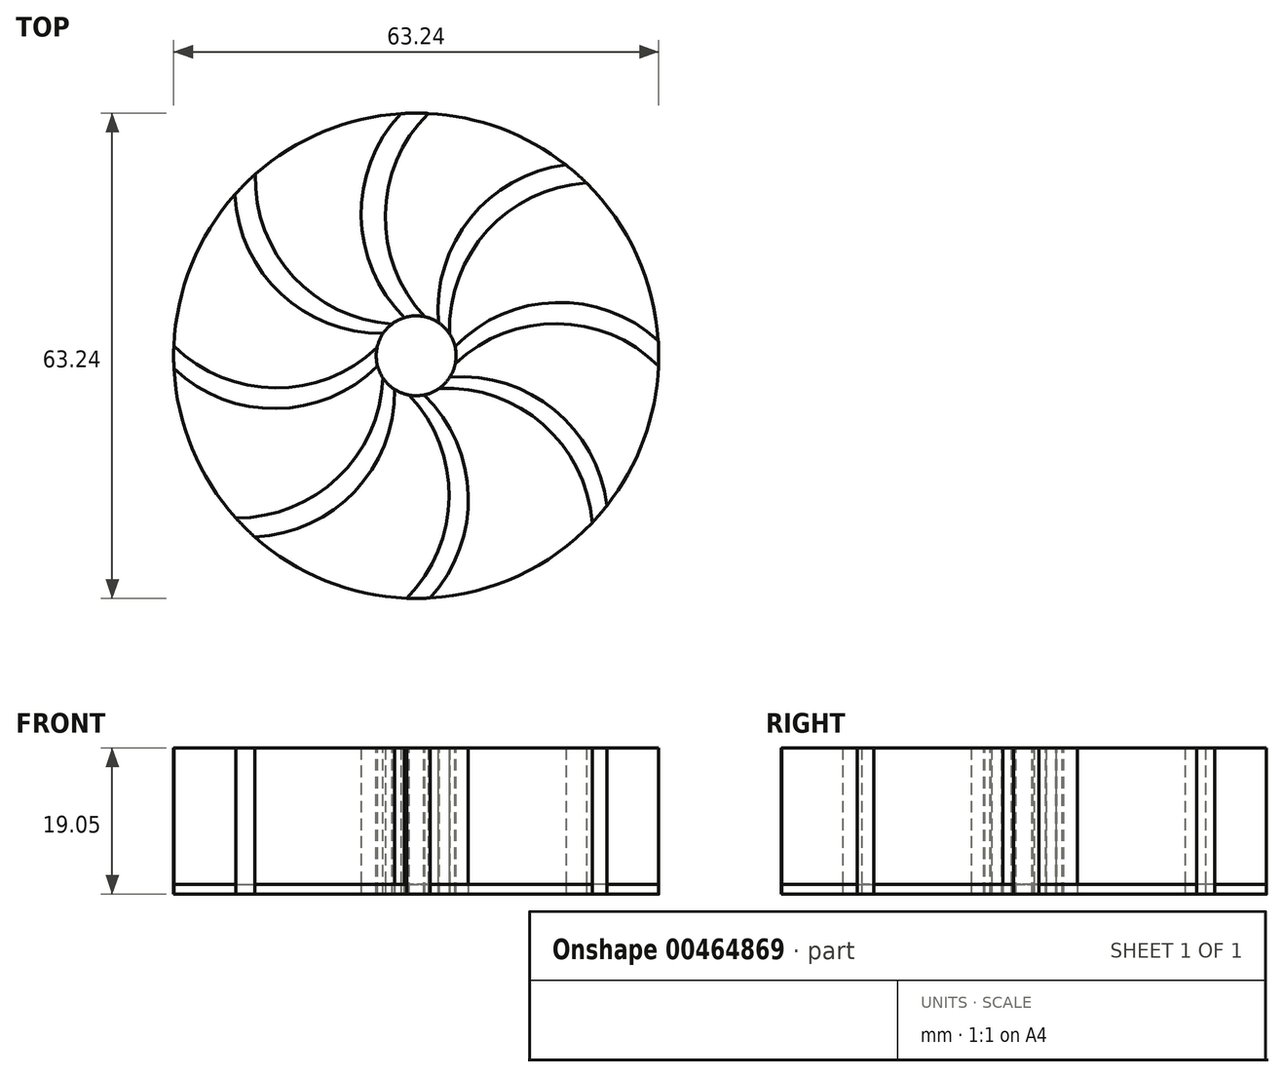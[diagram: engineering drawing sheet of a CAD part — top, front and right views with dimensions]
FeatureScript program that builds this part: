
annotation { "Feature Type Name" : "Feature", "Feature Type Description" : "" }
export const myFeature = defineFeature(function(context is Context, id is Id, definition is map)
    precondition{}
    {
        {
            var Q0;
            Q0=qCreatedBy(makeId("Top.planeOp"),FACE);
            var sketch = newSketch(context, id + "F0", { "sketchPlane" : qUnion([Q0])});
            skCircle(sketch, "E0", {"center": v(0, 0) * mm, "radius": 5.08 * mm});
            skPoint(sketch, "E1", {"position": v(-3.6, 3.6) * mm});
            skPoint(sketch, "E2", {"position": v(3.6, 3.6) * mm});
            skPoint(sketch, "E3", {"position": v(3.6, -3.6) * mm});
            skPoint(sketch, "E4", {"position": v(-3.6, -3.6) * mm});
            skArc(sketch, "E5", {"start": v(-31.6, 1.3) * mm, "mid": v(-18.28, -4.18) * mm, "end": v(-4.93, 1.22) * mm});
            skArc(sketch, "E6", {"start": v(-31.58, -1.67) * mm, "mid": v(-18.16, -6.88) * mm, "end": v(-4.93, -1.22) * mm});
            skArc(sketch, "E7", {"start": v(-31.58, -1.67) * mm, "mid": v(-29.22, -12.1) * mm, "end": v(-23.52, -21.13) * mm});
            skArc(sketch, "E8", {"start": v(-31.6, 1.3) * mm, "mid": v(-31.62, -0.19) * mm, "end": v(-31.58, -1.67) * mm});
            skArc(sketch, "E9", {"start": v(-23.52, -21.13) * mm, "mid": v(-22.31, -22.4) * mm, "end": v(-21.03, -23.61) * mm});
            skArc(sketch, "E10", {"start": v(-23.52, -21.13) * mm, "mid": v(-10.16, -15.82) * mm, "end": v(-4.32, -2.67) * mm});
            skArc(sketch, "E11", {"start": v(-21.03, -23.61) * mm, "mid": v(-11.82, -29.33) * mm, "end": v(-1.23, -31.6) * mm});
            skArc(sketch, "E12", {"start": v(-21.03, -23.61) * mm, "mid": v(-7.97, -17.64) * mm, "end": v(-2.8, -4.24) * mm});
            skLineSegment(sketch, "E13", {"start": v(-1.23, -31.6) * mm, "end": v(-1.23, -31.6) * mm});
            skArc(sketch, "E14", {"start": v(-1.23, -31.6) * mm, "mid": v(0.3, -31.62) * mm, "end": v(1.84, -31.57) * mm});
            skArc(sketch, "E15", {"start": v(-1.23, -31.6) * mm, "mid": v(4.3, -18.32) * mm, "end": v(-1.04, -4.97) * mm});
            skArc(sketch, "E16", {"start": v(1.84, -31.57) * mm, "mid": v(6.78, -18.1) * mm, "end": v(0.92, -5) * mm});
            skLineSegment(sketch, "E17", {"start": v(1.84, -31.57) * mm, "end": v(1.84, -31.57) * mm});
            skArc(sketch, "E18", {"start": v(1.84, -31.57) * mm, "mid": v(13.33, -28.67) * mm, "end": v(22.96, -21.75) * mm});
            skArc(sketch, "E19", {"start": v(22.96, -21.75) * mm, "mid": v(23.93, -20.68) * mm, "end": v(24.85, -19.56) * mm});
            skArc(sketch, "E20", {"start": v(22.96, -21.75) * mm, "mid": v(16.45, -8.87) * mm, "end": v(2.79, -4.25) * mm});
            skArc(sketch, "E21", {"start": v(24.85, -19.56) * mm, "mid": v(17.94, -7) * mm, "end": v(4.23, -2.82) * mm});
            skArc(sketch, "E22", {"start": v(24.85, -19.56) * mm, "mid": v(29.66, -10.97) * mm, "end": v(31.6, -1.32) * mm});
            skArc(sketch, "E23", {"start": v(31.56, 1.96) * mm, "mid": v(28.78, 13.11) * mm, "end": v(22.2, 22.53) * mm});
            skLineSegment(sketch, "E24", {"start": v(31.56, 1.96) * mm, "end": v(31.56, 1.96) * mm});
            skArc(sketch, "E25", {"start": v(31.56, 1.96) * mm, "mid": v(18.09, 6.95) * mm, "end": v(4.96, 1.1) * mm});
            skArc(sketch, "E26", {"start": v(22.2, 22.53) * mm, "mid": v(9.2, 16.2) * mm, "end": v(4.37, 2.58) * mm});
            skArc(sketch, "E27", {"start": v(22.2, 22.53) * mm, "mid": v(20.89, 23.74) * mm, "end": v(19.52, 24.88) * mm});
            skArc(sketch, "E28", {"start": v(19.52, 24.88) * mm, "mid": v(11.07, 29.62) * mm, "end": v(1.58, 31.58) * mm});
            skArc(sketch, "E29", {"start": v(19.52, 24.88) * mm, "mid": v(7.02, 17.88) * mm, "end": v(2.94, 4.14) * mm});
            skArc(sketch, "E30", {"start": v(-2.02, 31.56) * mm, "mid": v(-12.16, 29.2) * mm, "end": v(-20.98, 23.66) * mm});
            skArc(sketch, "E31", {"start": v(1.58, 31.58) * mm, "mid": v(-0.22, 31.62) * mm, "end": v(-2.02, 31.56) * mm});
            skArc(sketch, "E32", {"start": v(1.58, 31.58) * mm, "mid": v(-4.02, 18.32) * mm, "end": v(1.26, 4.92) * mm});
            skArc(sketch, "E33", {"start": v(-2.02, 31.56) * mm, "mid": v(-7.17, 18.1) * mm, "end": v(-1.41, 4.88) * mm});
            skLineSegment(sketch, "E34", {"start": v(-20.98, 23.66) * mm, "end": v(-20.98, 23.66) * mm});
            skArc(sketch, "E35", {"start": v(-20.98, 23.66) * mm, "mid": v(-15.93, 10.23) * mm, "end": v(-2.94, 4.14) * mm});
            skArc(sketch, "E36", {"start": v(-20.98, 23.66) * mm, "mid": v(-22.35, 22.37) * mm, "end": v(-23.64, 21) * mm});
            skArc(sketch, "E37", {"start": v(-23.64, 21) * mm, "mid": v(-17.57, 8) * mm, "end": v(-4.15, 2.93) * mm});
            skArc(sketch, "E38", {"start": v(-23.64, 21) * mm, "mid": v(-29.32, 11.84) * mm, "end": v(-31.6, 1.3) * mm});
            skArc(sketch, "E39", {"start": v(31.6, -1.32) * mm, "mid": v(31.62, 0.32) * mm, "end": v(31.56, 1.96) * mm});
            skArc(sketch, "E40", {"start": v(31.6, -1.32) * mm, "mid": v(18.3, 4.2) * mm, "end": v(4.94, -1.17) * mm});
            skSolve(sketch);
        }
        {
            var Q0;
            {var subQ0=sQuery(id+"F0.wireOp",EDGE,"E35");Q0=makeQuery(id+"F0.imprint","IMPRINT",FACE,{"disambiguationData":[TD([[makeQuery(id+"F0.imprint","IMPRINT",EDGE,{"derivedFrom":subQ0}),-1.0]])]});}
            var Q1;
            Q1=makeQuery(id+"F0.imprint","IMPRINT",FACE,{"disambiguationData":[TD([[makeQuery(id+"F0.imprint","IMPRINT",EDGE,{"derivedFrom":sQuery(id+"F0.wireOp",EDGE,"E31")}),1.0]])]});
            var Q2;
            {var subQ0=sQuery(id+"F0.wireOp",EDGE,"E26");Q2=makeQuery(id+"F0.imprint","IMPRINT",FACE,{"disambiguationData":[TD([[makeQuery(id+"F0.imprint","IMPRINT",EDGE,{"derivedFrom":subQ0}),-1.0]])]});}
            var Q3;
            {var subQ0=sQuery(id+"F0.wireOp",EDGE,"E25");Q3=makeQuery(id+"F0.imprint","IMPRINT",FACE,{"disambiguationData":[TD([[makeQuery(id+"F0.imprint","IMPRINT",EDGE,{"derivedFrom":subQ0}),1.0]])]});}
            var Q4;
            Q4=makeQuery(id+"F0.imprint","IMPRINT",FACE,{"disambiguationData":[TD([[makeQuery(id+"F0.imprint","IMPRINT",EDGE,{"derivedFrom":sQuery(id+"F0.wireOp",EDGE,"E19")}),1.0]])]});
            var Q5;
            Q5=makeQuery(id+"F0.imprint","IMPRINT",FACE,{"disambiguationData":[TD([[makeQuery(id+"F0.imprint","IMPRINT",EDGE,{"derivedFrom":sQuery(id+"F0.wireOp",EDGE,"E14")}),1.0]])]});
            var Q6;
            Q6=makeQuery(id+"F0.imprint","IMPRINT",FACE,{"disambiguationData":[TD([[makeQuery(id+"F0.imprint","IMPRINT",EDGE,{"derivedFrom":sQuery(id+"F0.wireOp",EDGE,"E9")}),1.0]])]});
            var Q7;
            {var subQ0=sQuery(id+"F0.wireOp",EDGE,"E5");Q7=makeQuery(id+"F0.imprint","IMPRINT",FACE,{"disambiguationData":[TD([[makeQuery(id+"F0.imprint","IMPRINT",EDGE,{"derivedFrom":subQ0}),-1.0]])]});}
            extrude(context, id + "F1", {"entities" : qUnion([Q0, Q1, Q2, Q3, Q4, Q5, Q6, Q7]), "depth" : 19.05 * mm});
        }
        {
            var Q0;
            {var subQ0=sQuery(id+"F0.wireOp",EDGE,"E5");Q0=makeQuery(id+"F0.imprint","IMPRINT",FACE,{"disambiguationData":[TD([[makeQuery(id+"F0.imprint","IMPRINT",EDGE,{"derivedFrom":subQ0}),1.0]])]});}
            var Q1;
            Q1=makeQuery(id+"F0.imprint","IMPRINT",FACE,{"disambiguationData":[TD([[makeQuery(id+"F0.imprint","IMPRINT",EDGE,{"derivedFrom":sQuery(id+"F0.wireOp",EDGE,"E30")}),1.0]])]});
            var Q2;
            Q2=makeQuery(id+"F0.imprint","IMPRINT",FACE,{"disambiguationData":[TD([[makeQuery(id+"F0.imprint","IMPRINT",EDGE,{"derivedFrom":sQuery(id+"F0.wireOp",EDGE,"E28")}),1.0]])]});
            var Q3;
            Q3=makeQuery(id+"F0.imprint","IMPRINT",FACE,{"disambiguationData":[TD([[makeQuery(id+"F0.imprint","IMPRINT",EDGE,{"derivedFrom":sQuery(id+"F0.wireOp",EDGE,"E23")}),1.0]])]});
            var Q4;
            {var subQ0=sQuery(id+"F0.wireOp",EDGE,"E21");Q4=makeQuery(id+"F0.imprint","IMPRINT",FACE,{"disambiguationData":[TD([[makeQuery(id+"F0.imprint","IMPRINT",EDGE,{"derivedFrom":subQ0}),-1.0]])]});}
            var Q5;
            {var subQ0=sQuery(id+"F0.wireOp",EDGE,"E16");Q5=makeQuery(id+"F0.imprint","IMPRINT",FACE,{"disambiguationData":[TD([[makeQuery(id+"F0.imprint","IMPRINT",EDGE,{"derivedFrom":subQ0}),-1.0]])]});}
            var Q6;
            Q6=makeQuery(id+"F0.imprint","IMPRINT",FACE,{"disambiguationData":[TD([[makeQuery(id+"F0.imprint","IMPRINT",EDGE,{"derivedFrom":sQuery(id+"F0.wireOp",EDGE,"E11")}),1.0]])]});
            var Q7;
            {var subQ0=sQuery(id+"F0.wireOp",EDGE,"E6");Q7=makeQuery(id+"F0.imprint","IMPRINT",FACE,{"disambiguationData":[TD([[makeQuery(id+"F0.imprint","IMPRINT",EDGE,{"derivedFrom":subQ0}),-1.0]])]});}
            extrude(context, id + "F2", {"entities" : qUnion([Q0, Q1, Q2, Q3, Q4, Q5, Q6, Q7]), "depth" : 1.27 * mm});
        }
        {
            var Q0;
            Q0=makeQuery(id+"F1.opExtrude","CAP_FACE",FACE,{"disambiguationData":[OSD([sQuery(id+"F0.wireOp",EDGE,"E0"),sQuery(id+"F0.wireOp",EDGE,"E5"),sQuery(id+"F0.wireOp",EDGE,"E6"),sQuery(id+"F0.wireOp",EDGE,"E8")])],"isStart":false});
            var sketch = newSketch(context, id + "F3", { "sketchPlane" : qUnion([Q0])});
            skCircle(sketch, "E41", {"center": v(0, 0) * mm, "radius": 5.2 * mm});
            skSolve(sketch);
        }
        {
            var Q0;
            Q0=sQuery(id+"F3.wireOp",VERTEX,"E41.center");
            var Q1;
            Q1=makeQuery(id+"F1.opExtrude","SWEPT_BODY",BODY,{"disambiguationData":[OSD([sQuery(id+"F0.wireOp",EDGE,"E0"),sQuery(id+"F0.wireOp",EDGE,"E26"),sQuery(id+"F0.wireOp",EDGE,"E27"),sQuery(id+"F0.wireOp",EDGE,"E29")])]});
            var Q2;
            Q2=makeQuery(id+"F1.opExtrude","SWEPT_BODY",BODY,{"disambiguationData":[OSD([sQuery(id+"F0.wireOp",EDGE,"E0"),sQuery(id+"F0.wireOp",EDGE,"E31"),sQuery(id+"F0.wireOp",EDGE,"E32"),sQuery(id+"F0.wireOp",EDGE,"E33")])]});
            var Q3;
            Q3=makeQuery(id+"F1.opExtrude","SWEPT_BODY",BODY,{"disambiguationData":[OSD([sQuery(id+"F0.wireOp",EDGE,"E0"),sQuery(id+"F0.wireOp",EDGE,"E35"),sQuery(id+"F0.wireOp",EDGE,"E36"),sQuery(id+"F0.wireOp",EDGE,"E37")])]});
            var Q4;
            Q4=makeQuery(id+"F1.opExtrude","SWEPT_BODY",BODY,{"disambiguationData":[OSD([sQuery(id+"F0.wireOp",EDGE,"E0"),sQuery(id+"F0.wireOp",EDGE,"E5"),sQuery(id+"F0.wireOp",EDGE,"E6"),sQuery(id+"F0.wireOp",EDGE,"E8")])]});
            var Q5;
            Q5=makeQuery(id+"F1.opExtrude","SWEPT_BODY",BODY,{"disambiguationData":[OSD([sQuery(id+"F0.wireOp",EDGE,"E0"),sQuery(id+"F0.wireOp",EDGE,"E9"),sQuery(id+"F0.wireOp",EDGE,"E10"),sQuery(id+"F0.wireOp",EDGE,"E12")])]});
            var Q6;
            Q6=makeQuery(id+"F1.opExtrude","SWEPT_BODY",BODY,{"disambiguationData":[OSD([sQuery(id+"F0.wireOp",EDGE,"E0"),sQuery(id+"F0.wireOp",EDGE,"E14"),sQuery(id+"F0.wireOp",EDGE,"E15"),sQuery(id+"F0.wireOp",EDGE,"E16")])]});
            var Q7;
            Q7=makeQuery(id+"F1.opExtrude","SWEPT_BODY",BODY,{"disambiguationData":[OSD([sQuery(id+"F0.wireOp",EDGE,"E0"),sQuery(id+"F0.wireOp",EDGE,"E19"),sQuery(id+"F0.wireOp",EDGE,"E20"),sQuery(id+"F0.wireOp",EDGE,"E21")])]});
            var Q8;
            Q8=makeQuery(id+"F1.opExtrude","SWEPT_BODY",BODY,{"disambiguationData":[OSD([sQuery(id+"F0.wireOp",EDGE,"E0"),sQuery(id+"F0.wireOp",EDGE,"E25"),sQuery(id+"F0.wireOp",EDGE,"E39"),sQuery(id+"F0.wireOp",EDGE,"E40")])]});
            var Q9;
            Q9=makeQuery(id+"F2.opExtrude","SWEPT_BODY",BODY,{"disambiguationData":[OSD([sQuery(id+"F0.wireOp",EDGE,"E0"),sQuery(id+"F0.wireOp",EDGE,"E23"),sQuery(id+"F0.wireOp",EDGE,"E25"),sQuery(id+"F0.wireOp",EDGE,"E26")])]});
            var Q10;
            Q10=makeQuery(id+"F2.opExtrude","SWEPT_BODY",BODY,{"disambiguationData":[OSD([sQuery(id+"F0.wireOp",EDGE,"E0"),sQuery(id+"F0.wireOp",EDGE,"E28"),sQuery(id+"F0.wireOp",EDGE,"E29"),sQuery(id+"F0.wireOp",EDGE,"E32")])]});
            var Q11;
            Q11=makeQuery(id+"F2.opExtrude","SWEPT_BODY",BODY,{"disambiguationData":[OSD([sQuery(id+"F0.wireOp",EDGE,"E0"),sQuery(id+"F0.wireOp",EDGE,"E30"),sQuery(id+"F0.wireOp",EDGE,"E33"),sQuery(id+"F0.wireOp",EDGE,"E35")])]});
            var Q12;
            Q12=makeQuery(id+"F2.opExtrude","SWEPT_BODY",BODY,{"disambiguationData":[OSD([sQuery(id+"F0.wireOp",EDGE,"E0"),sQuery(id+"F0.wireOp",EDGE,"E5"),sQuery(id+"F0.wireOp",EDGE,"E37"),sQuery(id+"F0.wireOp",EDGE,"E38")])]});
            var Q13;
            Q13=makeQuery(id+"F2.opExtrude","SWEPT_BODY",BODY,{"disambiguationData":[OSD([sQuery(id+"F0.wireOp",EDGE,"E0"),sQuery(id+"F0.wireOp",EDGE,"E6"),sQuery(id+"F0.wireOp",EDGE,"E7"),sQuery(id+"F0.wireOp",EDGE,"E10")])]});
            var Q14;
            Q14=makeQuery(id+"F2.opExtrude","SWEPT_BODY",BODY,{"disambiguationData":[OSD([sQuery(id+"F0.wireOp",EDGE,"E0"),sQuery(id+"F0.wireOp",EDGE,"E11"),sQuery(id+"F0.wireOp",EDGE,"E12"),sQuery(id+"F0.wireOp",EDGE,"E15")])]});
            var Q15;
            Q15=makeQuery(id+"F2.opExtrude","SWEPT_BODY",BODY,{"disambiguationData":[OSD([sQuery(id+"F0.wireOp",EDGE,"E0"),sQuery(id+"F0.wireOp",EDGE,"E16"),sQuery(id+"F0.wireOp",EDGE,"E18"),sQuery(id+"F0.wireOp",EDGE,"E20")])]});
            var Q16;
            Q16=makeQuery(id+"F2.opExtrude","SWEPT_BODY",BODY,{"disambiguationData":[OSD([sQuery(id+"F0.wireOp",EDGE,"E0"),sQuery(id+"F0.wireOp",EDGE,"E21"),sQuery(id+"F0.wireOp",EDGE,"E22"),sQuery(id+"F0.wireOp",EDGE,"E40")])]});
            hole(context, id + "F4", {"style" : HoleStyle.SIMPLE, "endStyle" : HoleEndStyle.THROUGH, "holeDiameter" : 10.4 * mm, "isTappedThrough" : true, "tappedDepth" : 12.7 * mm, "tapClearance" : 3, "locations" : qUnion([Q0]), "scope" : qUnion([Q1, Q2, Q3, Q4, Q5, Q6, Q7, Q8, Q9, Q10, Q11, Q12, Q13, Q14, Q15, Q16])});
        }
    });
